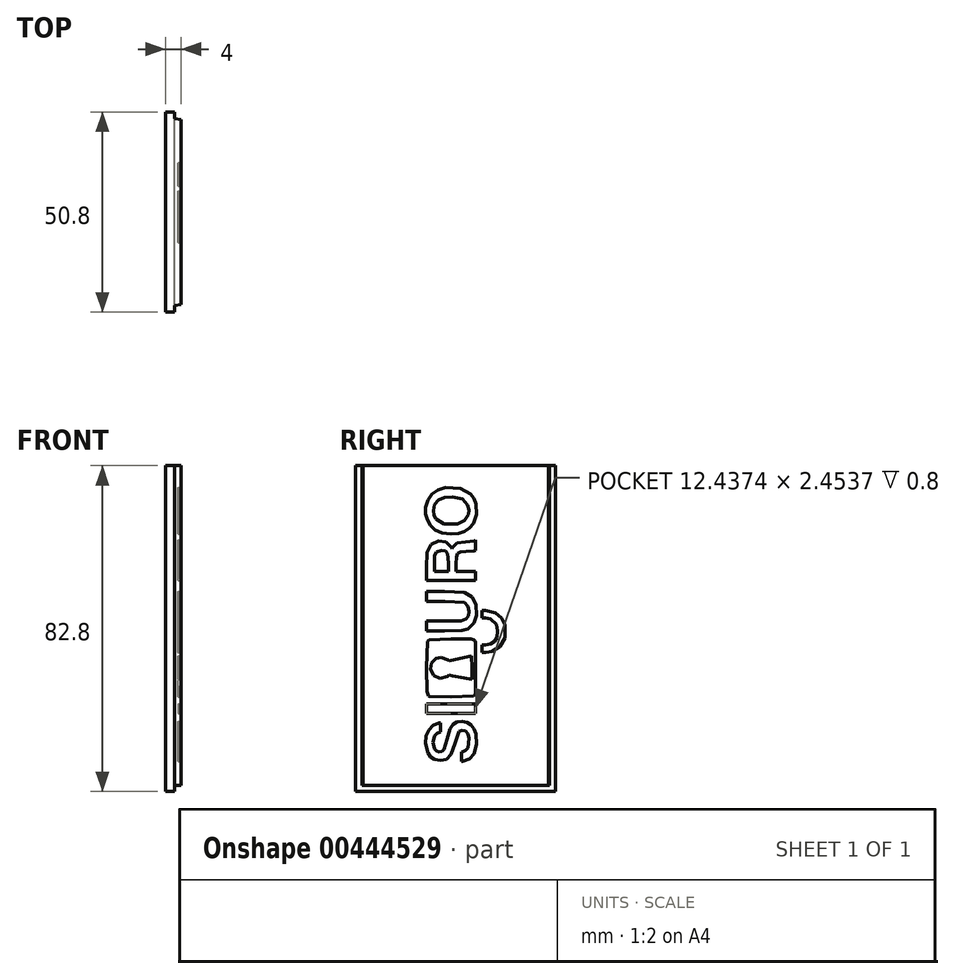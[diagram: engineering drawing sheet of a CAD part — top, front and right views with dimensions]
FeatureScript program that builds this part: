
annotation { "Feature Type Name" : "Feature", "Feature Type Description" : "" }
export const myFeature = defineFeature(function(context is Context, id is Id, definition is map)
    precondition{}
    {
        {
            var Q0;
            Q0=qCreatedBy(makeId("Top.planeOp"),FACE);
            var sketch = newSketch(context, id + "F0", { "sketchPlane" : qUnion([Q0])});
            skLineSegment(sketch, "E0.bottom", {"start": v(21.46, -52.97) * mm, "end": v(23.76, -52.97) * mm});
            skLineSegment(sketch, "E0.top", {"start": v(21.46, -2.17) * mm, "end": v(23.76, -2.17) * mm});
            skLineSegment(sketch, "E0.left", {"start": v(21.46, -52.97) * mm, "end": v(21.46, -2.17) * mm});
            skLineSegment(sketch, "E0.right", {"start": v(23.76, -52.97) * mm, "end": v(23.76, -2.17) * mm});
            skLineSegment(sketch, "E1", {"start": v(23.76, -52.97) * mm, "end": v(23.76, -51.37) * mm});
            skPoint(sketch, "E1.endSnap0", {"position": v(23.76, -27.57) * mm});
            skLineSegment(sketch, "E2", {"start": v(23.76, -51.37) * mm, "end": v(25.46, -51.37) * mm});
            skLineSegment(sketch, "E3", {"start": v(23.76, -2.17) * mm, "end": v(23.76, -3.77) * mm});
            skLineSegment(sketch, "E4", {"start": v(23.76, -3.77) * mm, "end": v(25.46, -3.77) * mm});
            skLineSegment(sketch, "E5", {"start": v(25.46, -51.37) * mm, "end": v(25.46, -3.77) * mm});
            skSolve(sketch);
        }
        {
            var Q0;
            Q0=makeQuery(id+"F0.imprint","IMPRINT",FACE,{"disambiguationData":[TD([[makeQuery(id+"F0.imprint","IMPRINT",EDGE,{"derivedFrom":sQuery(id+"F0.wireOp",EDGE,"E0.bottom")}),1.0]])]});
            var Q1;
            Q1=makeQuery(id+"F0.imprint","IMPRINT",FACE,{"disambiguationData":[TD([[makeQuery(id+"F0.imprint","IMPRINT",EDGE,{"derivedFrom":sQuery(id+"F0.wireOp",EDGE,"E0.right")}),-1.0]])]});
            extrude(context, id + "F1", {"entities" : qUnion([Q0, Q1]), "depth" : 82.8 * mm});
        }
        {
            var Q0;
            Q0=makeQuery(id+"F0.imprint","IMPRINT",FACE,{"disambiguationData":[TD([[makeQuery(id+"F0.imprint","IMPRINT",EDGE,{"derivedFrom":sQuery(id+"F0.wireOp",EDGE,"E0.right")}),-1.0]])]});
            extrude(context, id + "F2", {"entities" : qUnion([Q0]), "operationType" : NewBodyOperationType.REMOVE, "depth" : 1.5 * mm});
        }
        {
            var Q0;
            Q0=makeQuery(id+"F1.opExtrude","SWEPT_EDGE",EDGE,{"disambiguationData":[OSD([sQuery(id+"F0.wireOp",EDGE,"E2"),sQuery(id+"F0.wireOp",EDGE,"E5")])]});
            var Q1;
            Q1=makeQuery(id+"F2.boolean.opBoolean","COPY",EDGE,{"derivedFrom":makeQuery(id+"F2.opExtrude","CAP_EDGE",EDGE,{"disambiguationData":[OSD([sQuery(id+"F0.wireOp",EDGE,"E5")])],"isStart":false})});
            var Q2;
            Q2=makeQuery(id+"F1.opExtrude","SWEPT_EDGE",EDGE,{"disambiguationData":[OSD([sQuery(id+"F0.wireOp",EDGE,"E4"),sQuery(id+"F0.wireOp",EDGE,"E5")])]});
            chamfer(context, id + "F3", {"entities" : qUnion([Q0, Q1, Q2]), "chamferType" : ChamferType.OFFSET_ANGLE, "width" : 0.3 * mm, "oppositeDirection" : false, "angle" : 80 * degree, "tangentPropagation" : true});
        }
        {
            var Q0;
            Q0=makeQuery(id+"F1.opExtrude","SWEPT_FACE",FACE,{"disambiguationData":[OSD([sQuery(id+"F0.wireOp",EDGE,"E5")])]});
            var sketch = newSketch(context, id + "F4", { "sketchPlane" : qUnion([Q0])});
            skLineSegment(sketch, "E6", {"start": v(-14.78, 39.5) * mm, "end": v(-16, 36.81) * mm});
            skLineSegment(sketch, "E7", {"start": v(-16, 36.81) * mm, "end": v(-18.16, 35.38) * mm});
            skLineSegment(sketch, "E8", {"start": v(-18.16, 35.38) * mm, "end": v(-19.93, 35.18) * mm});
            skLineSegment(sketch, "E9", {"start": v(-19.93, 35.18) * mm, "end": v(-21.1, 35.18) * mm});
            skLineSegment(sketch, "E10", {"start": v(-21.1, 35.18) * mm, "end": v(-21.1, 36.32) * mm});
            skLineSegment(sketch, "E11", {"start": v(-21.1, 36.32) * mm, "end": v(-21.1, 37.46) * mm});
            skLineSegment(sketch, "E12", {"start": v(-21.1, 37.46) * mm, "end": v(-20.1, 37.5) * mm});
            skLineSegment(sketch, "E13", {"start": v(-20.1, 37.5) * mm, "end": v(-18.6, 37.79) * mm});
            skLineSegment(sketch, "E14", {"start": v(-18.6, 37.79) * mm, "end": v(-17.35, 39.11) * mm});
            skLineSegment(sketch, "E15", {"start": v(-17.35, 39.11) * mm, "end": v(-17.13, 40.68) * mm});
            skLineSegment(sketch, "E16", {"start": v(-17.13, 40.68) * mm, "end": v(-17.35, 42.25) * mm});
            skLineSegment(sketch, "E17", {"start": v(-17.35, 42.25) * mm, "end": v(-18.69, 43.58) * mm});
            skLineSegment(sketch, "E18", {"start": v(-18.69, 43.58) * mm, "end": v(-20.13, 43.85) * mm});
            skLineSegment(sketch, "E19", {"start": v(-20.13, 43.85) * mm, "end": v(-21.1, 43.9) * mm});
            skLineSegment(sketch, "E20", {"start": v(-21.1, 43.9) * mm, "end": v(-21.1, 45.04) * mm});
            skLineSegment(sketch, "E21", {"start": v(-21.1, 45.04) * mm, "end": v(-21.1, 46.18) * mm});
            skLineSegment(sketch, "E22", {"start": v(-21.1, 46.18) * mm, "end": v(-20, 46.17) * mm});
            skLineSegment(sketch, "E23", {"start": v(-20, 46.17) * mm, "end": v(-18.32, 45.99) * mm});
            skLineSegment(sketch, "E24", {"start": v(-18.32, 45.99) * mm, "end": v(-16.24, 44.73) * mm});
            skLineSegment(sketch, "E25", {"start": v(-16.24, 44.73) * mm, "end": v(-14.97, 42.67) * mm});
            skLineSegment(sketch, "E26", {"start": v(-14.97, 42.67) * mm, "end": v(-14.76, 40.93) * mm});
            skLineSegment(sketch, "E27", {"start": v(-14.76, 40.93) * mm, "end": v(-14.78, 39.5) * mm});
            skLineSegment(sketch, "E28", {"start": v(-14.78, 39.5) * mm, "end": v(-14.78, 39.5) * mm});
            skLineSegment(sketch, "E29", {"start": v(-15.1, 42.37) * mm, "end": v(-16, 44.13) * mm});
            skLineSegment(sketch, "E30", {"start": v(-16, 44.13) * mm, "end": v(-17.48, 45.4) * mm});
            skLineSegment(sketch, "E31", {"start": v(-17.48, 45.4) * mm, "end": v(-19.99, 45.97) * mm});
            skLineSegment(sketch, "E32", {"start": v(-19.99, 45.97) * mm, "end": v(-20.9, 45.97) * mm});
            skLineSegment(sketch, "E33", {"start": v(-20.9, 45.97) * mm, "end": v(-20.9, 45) * mm});
            skLineSegment(sketch, "E34", {"start": v(-20.9, 45) * mm, "end": v(-20.9, 44.02) * mm});
            skLineSegment(sketch, "E35", {"start": v(-20.9, 44.02) * mm, "end": v(-20.06, 44.02) * mm});
            skLineSegment(sketch, "E36", {"start": v(-20.06, 44.02) * mm, "end": v(-18.75, 43.85) * mm});
            skLineSegment(sketch, "E37", {"start": v(-18.75, 43.85) * mm, "end": v(-17.2, 42.43) * mm});
            skLineSegment(sketch, "E38", {"start": v(-17.2, 42.43) * mm, "end": v(-16.94, 40.8) * mm});
            skLineSegment(sketch, "E39", {"start": v(-16.94, 40.8) * mm, "end": v(-17.09, 39.19) * mm});
            skLineSegment(sketch, "E40", {"start": v(-17.09, 39.19) * mm, "end": v(-17.76, 38.12) * mm});
            skLineSegment(sketch, "E41", {"start": v(-17.76, 38.12) * mm, "end": v(-18.8, 37.46) * mm});
            skLineSegment(sketch, "E42", {"start": v(-18.8, 37.46) * mm, "end": v(-20.03, 37.28) * mm});
            skLineSegment(sketch, "E43", {"start": v(-20.03, 37.28) * mm, "end": v(-20.9, 37.23) * mm});
            skLineSegment(sketch, "E44", {"start": v(-20.9, 37.23) * mm, "end": v(-20.9, 36.25) * mm});
            skLineSegment(sketch, "E45", {"start": v(-20.9, 36.25) * mm, "end": v(-20.9, 35.28) * mm});
            skLineSegment(sketch, "E46", {"start": v(-20.9, 35.28) * mm, "end": v(-19.9, 35.33) * mm});
            skLineSegment(sketch, "E47", {"start": v(-19.9, 35.33) * mm, "end": v(-18.36, 35.55) * mm});
            skLineSegment(sketch, "E48", {"start": v(-18.36, 35.55) * mm, "end": v(-16.3, 36.84) * mm});
            skLineSegment(sketch, "E49", {"start": v(-16.3, 36.84) * mm, "end": v(-15.1, 38.95) * mm});
            skLineSegment(sketch, "E50", {"start": v(-15.1, 38.95) * mm, "end": v(-15.1, 42.37) * mm});
            skLineSegment(sketch, "E51", {"start": v(-0.1, -10) * mm, "end": v(-0.1, -10) * mm});
            skLineSegment(sketch, "E52", {"start": v(-22.14, 11.07) * mm, "end": v(-22.89, 9.2) * mm});
            skLineSegment(sketch, "E53", {"start": v(-22.89, 9.2) * mm, "end": v(-24.2, 7.95) * mm});
            skLineSegment(sketch, "E54", {"start": v(-24.2, 7.95) * mm, "end": v(-26, 7.47) * mm});
            skLineSegment(sketch, "E55", {"start": v(-26, 7.47) * mm, "end": v(-26.4, 7.47) * mm});
            skLineSegment(sketch, "E56", {"start": v(-26.4, 7.47) * mm, "end": v(-26.4, 8.81) * mm});
            skLineSegment(sketch, "E57", {"start": v(-26.4, 8.81) * mm, "end": v(-26.4, 10.15) * mm});
            skLineSegment(sketch, "E58", {"start": v(-26.4, 10.15) * mm, "end": v(-25.91, 10.26) * mm});
            skLineSegment(sketch, "E59", {"start": v(-25.91, 10.26) * mm, "end": v(-25.06, 10.73) * mm});
            skLineSegment(sketch, "E60", {"start": v(-25.06, 10.73) * mm, "end": v(-24.53, 11.58) * mm});
            skLineSegment(sketch, "E61", {"start": v(-24.53, 11.58) * mm, "end": v(-24.56, 14.2) * mm});
            skLineSegment(sketch, "E62", {"start": v(-24.56, 14.2) * mm, "end": v(-25.53, 15.23) * mm});
            skLineSegment(sketch, "E63", {"start": v(-25.53, 15.23) * mm, "end": v(-26.14, 15.25) * mm});
            skLineSegment(sketch, "E64", {"start": v(-26.14, 15.25) * mm, "end": v(-26.68, 14.9) * mm});
            skLineSegment(sketch, "E65", {"start": v(-26.68, 14.9) * mm, "end": v(-27.61, 11.97) * mm});
            skLineSegment(sketch, "E66", {"start": v(-27.61, 11.97) * mm, "end": v(-28.26, 9.72) * mm});
            skLineSegment(sketch, "E67", {"start": v(-28.26, 9.72) * mm, "end": v(-29.5, 8.15) * mm});
            skLineSegment(sketch, "E68", {"start": v(-29.5, 8.15) * mm, "end": v(-31.5, 7.64) * mm});
            skLineSegment(sketch, "E69", {"start": v(-31.5, 7.64) * mm, "end": v(-32.86, 7.87) * mm});
            skLineSegment(sketch, "E70", {"start": v(-32.86, 7.87) * mm, "end": v(-33.99, 8.52) * mm});
            skLineSegment(sketch, "E71", {"start": v(-33.99, 8.52) * mm, "end": v(-34.83, 9.57) * mm});
            skLineSegment(sketch, "E72", {"start": v(-34.83, 9.57) * mm, "end": v(-35.33, 10.95) * mm});
            skLineSegment(sketch, "E73", {"start": v(-35.33, 10.95) * mm, "end": v(-35.46, 12.63) * mm});
            skLineSegment(sketch, "E74", {"start": v(-35.46, 12.63) * mm, "end": v(-35.12, 14.9) * mm});
            skLineSegment(sketch, "E75", {"start": v(-35.12, 14.9) * mm, "end": v(-34.05, 16.51) * mm});
            skLineSegment(sketch, "E76", {"start": v(-34.05, 16.51) * mm, "end": v(-32.83, 17.33) * mm});
            skLineSegment(sketch, "E77", {"start": v(-32.83, 17.33) * mm, "end": v(-31.54, 17.62) * mm});
            skLineSegment(sketch, "E78", {"start": v(-31.54, 17.62) * mm, "end": v(-31.22, 17.62) * mm});
            skLineSegment(sketch, "E79", {"start": v(-31.22, 17.62) * mm, "end": v(-31.22, 16.27) * mm});
            skLineSegment(sketch, "E80", {"start": v(-31.22, 16.27) * mm, "end": v(-31.22, 14.92) * mm});
            skLineSegment(sketch, "E81", {"start": v(-31.22, 14.92) * mm, "end": v(-31.45, 14.87) * mm});
            skLineSegment(sketch, "E82", {"start": v(-31.45, 14.87) * mm, "end": v(-32.64, 14.16) * mm});
            skLineSegment(sketch, "E83", {"start": v(-32.64, 14.16) * mm, "end": v(-33.08, 12.36) * mm});
            skLineSegment(sketch, "E84", {"start": v(-33.08, 12.36) * mm, "end": v(-32.54, 10.71) * mm});
            skLineSegment(sketch, "E85", {"start": v(-32.54, 10.71) * mm, "end": v(-31.64, 10.35) * mm});
            skLineSegment(sketch, "E86", {"start": v(-31.64, 10.35) * mm, "end": v(-30.8, 10.78) * mm});
            skLineSegment(sketch, "E87", {"start": v(-30.8, 10.78) * mm, "end": v(-30.07, 13.24) * mm});
            skLineSegment(sketch, "E88", {"start": v(-30.07, 13.24) * mm, "end": v(-29.2, 16.16) * mm});
            skLineSegment(sketch, "E89", {"start": v(-29.2, 16.16) * mm, "end": v(-28.1, 17.53) * mm});
            skLineSegment(sketch, "E90", {"start": v(-28.1, 17.53) * mm, "end": v(-26.44, 18.03) * mm});
            skLineSegment(sketch, "E91", {"start": v(-26.44, 18.03) * mm, "end": v(-24.73, 17.8) * mm});
            skLineSegment(sketch, "E92", {"start": v(-24.73, 17.8) * mm, "end": v(-23.36, 16.97) * mm});
            skLineSegment(sketch, "E93", {"start": v(-23.36, 16.97) * mm, "end": v(-22.13, 14.48) * mm});
            skLineSegment(sketch, "E94", {"start": v(-22.13, 14.48) * mm, "end": v(-22.14, 11.07) * mm});
            skLineSegment(sketch, "E95", {"start": v(-31.4, -2.97) * mm, "end": v(-31.4, -2.97) * mm});
            skLineSegment(sketch, "E96", {"start": v(-22.38, 14.56) * mm, "end": v(-22.88, 15.85) * mm});
            skLineSegment(sketch, "E97", {"start": v(-22.88, 15.85) * mm, "end": v(-23.65, 16.85) * mm});
            skLineSegment(sketch, "E98", {"start": v(-23.65, 16.85) * mm, "end": v(-24.68, 17.54) * mm});
            skLineSegment(sketch, "E99", {"start": v(-24.68, 17.54) * mm, "end": v(-26.02, 17.77) * mm});
            skLineSegment(sketch, "E100", {"start": v(-26.02, 17.77) * mm, "end": v(-27.31, 17.65) * mm});
            skLineSegment(sketch, "E101", {"start": v(-27.31, 17.65) * mm, "end": v(-28.28, 17.05) * mm});
            skLineSegment(sketch, "E102", {"start": v(-28.28, 17.05) * mm, "end": v(-29.05, 15.87) * mm});
            skLineSegment(sketch, "E103", {"start": v(-29.05, 15.87) * mm, "end": v(-29.83, 13.2) * mm});
            skLineSegment(sketch, "E104", {"start": v(-29.83, 13.2) * mm, "end": v(-30.58, 10.66) * mm});
            skLineSegment(sketch, "E105", {"start": v(-30.58, 10.66) * mm, "end": v(-31.12, 10.21) * mm});
            skLineSegment(sketch, "E106", {"start": v(-31.12, 10.21) * mm, "end": v(-31.8, 10.1) * mm});
            skLineSegment(sketch, "E107", {"start": v(-31.8, 10.1) * mm, "end": v(-32.48, 10.33) * mm});
            skLineSegment(sketch, "E108", {"start": v(-32.48, 10.33) * mm, "end": v(-32.98, 10.87) * mm});
            skLineSegment(sketch, "E109", {"start": v(-32.98, 10.87) * mm, "end": v(-33.31, 12.47) * mm});
            skLineSegment(sketch, "E110", {"start": v(-33.31, 12.47) * mm, "end": v(-33, 14.05) * mm});
            skLineSegment(sketch, "E111", {"start": v(-33, 14.05) * mm, "end": v(-32.35, 14.78) * mm});
            skLineSegment(sketch, "E112", {"start": v(-32.35, 14.78) * mm, "end": v(-31.5, 15.09) * mm});
            skLineSegment(sketch, "E113", {"start": v(-31.5, 15.09) * mm, "end": v(-31.39, 16.26) * mm});
            skLineSegment(sketch, "E114", {"start": v(-31.39, 16.26) * mm, "end": v(-31.39, 17.43) * mm});
            skLineSegment(sketch, "E115", {"start": v(-31.39, 17.43) * mm, "end": v(-31.86, 17.35) * mm});
            skLineSegment(sketch, "E116", {"start": v(-31.86, 17.35) * mm, "end": v(-33.33, 16.8) * mm});
            skLineSegment(sketch, "E117", {"start": v(-33.33, 16.8) * mm, "end": v(-34.42, 15.7) * mm});
            skLineSegment(sketch, "E118", {"start": v(-34.42, 15.7) * mm, "end": v(-35.09, 14.14) * mm});
            skLineSegment(sketch, "E119", {"start": v(-35.09, 14.14) * mm, "end": v(-35.25, 12.24) * mm});
            skLineSegment(sketch, "E120", {"start": v(-35.25, 12.24) * mm, "end": v(-34.63, 9.74) * mm});
            skLineSegment(sketch, "E121", {"start": v(-34.63, 9.74) * mm, "end": v(-33.96, 8.84) * mm});
            skLineSegment(sketch, "E122", {"start": v(-33.96, 8.84) * mm, "end": v(-33.01, 8.2) * mm});
            skLineSegment(sketch, "E123", {"start": v(-33.01, 8.2) * mm, "end": v(-31.43, 7.94) * mm});
            skLineSegment(sketch, "E124", {"start": v(-31.43, 7.94) * mm, "end": v(-29.94, 8.17) * mm});
            skLineSegment(sketch, "E125", {"start": v(-29.94, 8.17) * mm, "end": v(-28.72, 9.37) * mm});
            skLineSegment(sketch, "E126", {"start": v(-28.72, 9.37) * mm, "end": v(-27.8, 12.24) * mm});
            skLineSegment(sketch, "E127", {"start": v(-27.8, 12.24) * mm, "end": v(-26.73, 15.22) * mm});
            skLineSegment(sketch, "E128", {"start": v(-26.73, 15.22) * mm, "end": v(-25.95, 15.49) * mm});
            skLineSegment(sketch, "E129", {"start": v(-25.95, 15.49) * mm, "end": v(-25.09, 15.32) * mm});
            skLineSegment(sketch, "E130", {"start": v(-25.09, 15.32) * mm, "end": v(-24.5, 14.62) * mm});
            skLineSegment(sketch, "E131", {"start": v(-24.5, 14.62) * mm, "end": v(-24.18, 13.5) * mm});
            skLineSegment(sketch, "E132", {"start": v(-24.18, 13.5) * mm, "end": v(-24.5, 11.05) * mm});
            skLineSegment(sketch, "E133", {"start": v(-24.5, 11.05) * mm, "end": v(-25.05, 10.38) * mm});
            skLineSegment(sketch, "E134", {"start": v(-25.05, 10.38) * mm, "end": v(-25.83, 10.04) * mm});
            skLineSegment(sketch, "E135", {"start": v(-25.83, 10.04) * mm, "end": v(-26.14, 9.99) * mm});
            skLineSegment(sketch, "E136", {"start": v(-26.14, 9.99) * mm, "end": v(-26.14, 8.82) * mm});
            skLineSegment(sketch, "E137", {"start": v(-26.14, 8.82) * mm, "end": v(-26.14, 7.64) * mm});
            skLineSegment(sketch, "E138", {"start": v(-26.14, 7.64) * mm, "end": v(-25.87, 7.69) * mm});
            skLineSegment(sketch, "E139", {"start": v(-25.87, 7.69) * mm, "end": v(-24.13, 8.3) * mm});
            skLineSegment(sketch, "E140", {"start": v(-24.13, 8.3) * mm, "end": v(-22.97, 9.54) * mm});
            skLineSegment(sketch, "E141", {"start": v(-22.97, 9.54) * mm, "end": v(-22.25, 11.9) * mm});
            skLineSegment(sketch, "E142", {"start": v(-22.25, 11.9) * mm, "end": v(-22.38, 14.56) * mm});
            skLineSegment(sketch, "E143", {"start": v(-22.13, 44.1) * mm, "end": v(-23.35, 41.76) * mm});
            skLineSegment(sketch, "E144", {"start": v(-23.35, 41.76) * mm, "end": v(-24.31, 41.06) * mm});
            skLineSegment(sketch, "E145", {"start": v(-24.31, 41.06) * mm, "end": v(-26.02, 40.63) * mm});
            skLineSegment(sketch, "E146", {"start": v(-26.02, 40.63) * mm, "end": v(-30.71, 40.57) * mm});
            skLineSegment(sketch, "E147", {"start": v(-30.71, 40.57) * mm, "end": v(-35.15, 40.6) * mm});
            skLineSegment(sketch, "E148", {"start": v(-35.15, 40.6) * mm, "end": v(-35.15, 42) * mm});
            skLineSegment(sketch, "E149", {"start": v(-35.15, 42) * mm, "end": v(-35.15, 43.39) * mm});
            skLineSegment(sketch, "E150", {"start": v(-35.15, 43.39) * mm, "end": v(-30.67, 43.43) * mm});
            skLineSegment(sketch, "E151", {"start": v(-30.67, 43.43) * mm, "end": v(-26.19, 43.56) * mm});
            skLineSegment(sketch, "E152", {"start": v(-26.19, 43.56) * mm, "end": v(-25, 44.14) * mm});
            skLineSegment(sketch, "E153", {"start": v(-25, 44.14) * mm, "end": v(-24.45, 45.73) * mm});
            skLineSegment(sketch, "E154", {"start": v(-24.45, 45.73) * mm, "end": v(-24.72, 47.05) * mm});
            skLineSegment(sketch, "E155", {"start": v(-24.72, 47.05) * mm, "end": v(-25.54, 47.82) * mm});
            skLineSegment(sketch, "E156", {"start": v(-25.54, 47.82) * mm, "end": v(-26.02, 48.04) * mm});
            skLineSegment(sketch, "E157", {"start": v(-26.02, 48.04) * mm, "end": v(-30.59, 48.08) * mm});
            skLineSegment(sketch, "E158", {"start": v(-30.59, 48.08) * mm, "end": v(-35.15, 48.13) * mm});
            skLineSegment(sketch, "E159", {"start": v(-35.15, 48.13) * mm, "end": v(-35.15, 49.52) * mm});
            skLineSegment(sketch, "E160", {"start": v(-35.15, 49.52) * mm, "end": v(-35.15, 50.92) * mm});
            skLineSegment(sketch, "E161", {"start": v(-35.15, 50.92) * mm, "end": v(-30.6, 50.94) * mm});
            skLineSegment(sketch, "E162", {"start": v(-30.6, 50.94) * mm, "end": v(-25.94, 50.89) * mm});
            skLineSegment(sketch, "E163", {"start": v(-25.94, 50.89) * mm, "end": v(-24.28, 50.44) * mm});
            skLineSegment(sketch, "E164", {"start": v(-24.28, 50.44) * mm, "end": v(-22.91, 49.24) * mm});
            skLineSegment(sketch, "E165", {"start": v(-22.91, 49.24) * mm, "end": v(-22.13, 47.39) * mm});
            skLineSegment(sketch, "E166", {"start": v(-22.13, 47.39) * mm, "end": v(-22.13, 44.1) * mm});
            skLineSegment(sketch, "E167", {"start": v(-22.13, 44.1) * mm, "end": v(-22.13, 44.1) * mm});
            skLineSegment(sketch, "E168", {"start": v(-22.38, 47.45) * mm, "end": v(-23.44, 49.47) * mm});
            skLineSegment(sketch, "E169", {"start": v(-23.44, 49.47) * mm, "end": v(-25.35, 50.6) * mm});
            skLineSegment(sketch, "E170", {"start": v(-25.35, 50.6) * mm, "end": v(-30.4, 50.77) * mm});
            skLineSegment(sketch, "E171", {"start": v(-30.4, 50.77) * mm, "end": v(-34.94, 50.8) * mm});
            skLineSegment(sketch, "E172", {"start": v(-34.94, 50.8) * mm, "end": v(-34.94, 49.53) * mm});
            skLineSegment(sketch, "E173", {"start": v(-34.94, 49.53) * mm, "end": v(-34.94, 48.26) * mm});
            skLineSegment(sketch, "E174", {"start": v(-34.94, 48.26) * mm, "end": v(-30.31, 48.23) * mm});
            skLineSegment(sketch, "E175", {"start": v(-30.31, 48.23) * mm, "end": v(-25.34, 48.03) * mm});
            skLineSegment(sketch, "E176", {"start": v(-25.34, 48.03) * mm, "end": v(-24.44, 47.02) * mm});
            skLineSegment(sketch, "E177", {"start": v(-24.44, 47.02) * mm, "end": v(-24.24, 45.71) * mm});
            skLineSegment(sketch, "E178", {"start": v(-24.24, 45.71) * mm, "end": v(-24.38, 44.57) * mm});
            skLineSegment(sketch, "E179", {"start": v(-24.38, 44.57) * mm, "end": v(-24.96, 43.83) * mm});
            skLineSegment(sketch, "E180", {"start": v(-24.96, 43.83) * mm, "end": v(-26.2, 43.34) * mm});
            skLineSegment(sketch, "E181", {"start": v(-26.2, 43.34) * mm, "end": v(-30.61, 43.26) * mm});
            skLineSegment(sketch, "E182", {"start": v(-30.61, 43.26) * mm, "end": v(-34.94, 43.26) * mm});
            skLineSegment(sketch, "E183", {"start": v(-34.94, 43.26) * mm, "end": v(-34.94, 42.03) * mm});
            skLineSegment(sketch, "E184", {"start": v(-34.94, 42.03) * mm, "end": v(-34.94, 40.8) * mm});
            skLineSegment(sketch, "E185", {"start": v(-34.94, 40.8) * mm, "end": v(-30.48, 40.8) * mm});
            skLineSegment(sketch, "E186", {"start": v(-30.48, 40.8) * mm, "end": v(-25.97, 40.88) * mm});
            skLineSegment(sketch, "E187", {"start": v(-25.97, 40.88) * mm, "end": v(-24.41, 41.28) * mm});
            skLineSegment(sketch, "E188", {"start": v(-24.41, 41.28) * mm, "end": v(-22.9, 42.75) * mm});
            skLineSegment(sketch, "E189", {"start": v(-22.9, 42.75) * mm, "end": v(-22.25, 44.69) * mm});
            skLineSegment(sketch, "E190", {"start": v(-22.25, 44.69) * mm, "end": v(-22.38, 47.45) * mm});
            skLineSegment(sketch, "E191", {"start": v(4.98, -2.73) * mm, "end": v(4.98, -2.73) * mm});
            skLineSegment(sketch, "E192", {"start": v(-22.12, 69.86) * mm, "end": v(-22.69, 68.28) * mm});
            skLineSegment(sketch, "E193", {"start": v(-22.69, 68.28) * mm, "end": v(-23.6, 67.01) * mm});
            skLineSegment(sketch, "E194", {"start": v(-23.6, 67.01) * mm, "end": v(-24.86, 66.05) * mm});
            skLineSegment(sketch, "E195", {"start": v(-24.86, 66.05) * mm, "end": v(-26.44, 65.41) * mm});
            skLineSegment(sketch, "E196", {"start": v(-26.44, 65.41) * mm, "end": v(-28.72, 65.23) * mm});
            skLineSegment(sketch, "E197", {"start": v(-28.72, 65.23) * mm, "end": v(-30.8, 65.36) * mm});
            skLineSegment(sketch, "E198", {"start": v(-30.8, 65.36) * mm, "end": v(-32.4, 65.95) * mm});
            skLineSegment(sketch, "E199", {"start": v(-32.4, 65.95) * mm, "end": v(-33.8, 66.98) * mm});
            skLineSegment(sketch, "E200", {"start": v(-33.8, 66.98) * mm, "end": v(-35.06, 68.9) * mm});
            skLineSegment(sketch, "E201", {"start": v(-35.06, 68.9) * mm, "end": v(-35.46, 71.34) * mm});
            skLineSegment(sketch, "E202", {"start": v(-35.46, 71.34) * mm, "end": v(-34.8, 74.31) * mm});
            skLineSegment(sketch, "E203", {"start": v(-34.8, 74.31) * mm, "end": v(-33.31, 76.18) * mm});
            skLineSegment(sketch, "E204", {"start": v(-33.31, 76.18) * mm, "end": v(-31, 77.29) * mm});
            skLineSegment(sketch, "E205", {"start": v(-31, 77.29) * mm, "end": v(-28.72, 77.47) * mm});
            skLineSegment(sketch, "E206", {"start": v(-28.72, 77.47) * mm, "end": v(-26.44, 77.29) * mm});
            skLineSegment(sketch, "E207", {"start": v(-26.44, 77.29) * mm, "end": v(-23.79, 75.86) * mm});
            skLineSegment(sketch, "E208", {"start": v(-23.79, 75.86) * mm, "end": v(-22.88, 74.74) * mm});
            skLineSegment(sketch, "E209", {"start": v(-22.88, 74.74) * mm, "end": v(-22.25, 73.34) * mm});
            skLineSegment(sketch, "E210", {"start": v(-22.25, 73.34) * mm, "end": v(-22.12, 69.86) * mm});
            skLineSegment(sketch, "E211", {"start": v(-22.43, 73.05) * mm, "end": v(-23, 74.45) * mm});
            skLineSegment(sketch, "E212", {"start": v(-23, 74.45) * mm, "end": v(-23.84, 75.58) * mm});
            skLineSegment(sketch, "E213", {"start": v(-23.84, 75.58) * mm, "end": v(-26.4, 77.02) * mm});
            skLineSegment(sketch, "E214", {"start": v(-26.4, 77.02) * mm, "end": v(-30.2, 77.2) * mm});
            skLineSegment(sketch, "E215", {"start": v(-30.2, 77.2) * mm, "end": v(-32.11, 76.62) * mm});
            skLineSegment(sketch, "E216", {"start": v(-32.11, 76.62) * mm, "end": v(-33.6, 75.59) * mm});
            skLineSegment(sketch, "E217", {"start": v(-33.6, 75.59) * mm, "end": v(-34.64, 74.1) * mm});
            skLineSegment(sketch, "E218", {"start": v(-34.64, 74.1) * mm, "end": v(-35.2, 72.2) * mm});
            skLineSegment(sketch, "E219", {"start": v(-35.2, 72.2) * mm, "end": v(-35.21, 70.54) * mm});
            skLineSegment(sketch, "E220", {"start": v(-35.21, 70.54) * mm, "end": v(-34.79, 68.94) * mm});
            skLineSegment(sketch, "E221", {"start": v(-34.79, 68.94) * mm, "end": v(-33.98, 67.54) * mm});
            skLineSegment(sketch, "E222", {"start": v(-33.98, 67.54) * mm, "end": v(-32.85, 66.48) * mm});
            skLineSegment(sketch, "E223", {"start": v(-32.85, 66.48) * mm, "end": v(-31.04, 65.68) * mm});
            skLineSegment(sketch, "E224", {"start": v(-31.04, 65.68) * mm, "end": v(-28.71, 65.43) * mm});
            skLineSegment(sketch, "E225", {"start": v(-28.71, 65.43) * mm, "end": v(-26.86, 65.58) * mm});
            skLineSegment(sketch, "E226", {"start": v(-26.86, 65.58) * mm, "end": v(-25.33, 66.06) * mm});
            skLineSegment(sketch, "E227", {"start": v(-25.33, 66.06) * mm, "end": v(-24.09, 66.89) * mm});
            skLineSegment(sketch, "E228", {"start": v(-24.09, 66.89) * mm, "end": v(-23.1, 68.06) * mm});
            skLineSegment(sketch, "E229", {"start": v(-23.1, 68.06) * mm, "end": v(-22.25, 70.42) * mm});
            skLineSegment(sketch, "E230", {"start": v(-22.25, 70.42) * mm, "end": v(-22.43, 73.05) * mm});
            skLineSegment(sketch, "E231", {"start": v(-24.3, 70.42) * mm, "end": v(-25.28, 68.85) * mm});
            skLineSegment(sketch, "E232", {"start": v(-25.28, 68.85) * mm, "end": v(-27.07, 67.95) * mm});
            skLineSegment(sketch, "E233", {"start": v(-27.07, 67.95) * mm, "end": v(-30.54, 68) * mm});
            skLineSegment(sketch, "E234", {"start": v(-30.54, 68) * mm, "end": v(-32.55, 69.22) * mm});
            skLineSegment(sketch, "E235", {"start": v(-32.55, 69.22) * mm, "end": v(-33.07, 70.18) * mm});
            skLineSegment(sketch, "E236", {"start": v(-33.07, 70.18) * mm, "end": v(-33.25, 71.35) * mm});
            skLineSegment(sketch, "E237", {"start": v(-33.25, 71.35) * mm, "end": v(-32.9, 72.9) * mm});
            skLineSegment(sketch, "E238", {"start": v(-32.9, 72.9) * mm, "end": v(-31.93, 74.05) * mm});
            skLineSegment(sketch, "E239", {"start": v(-31.93, 74.05) * mm, "end": v(-30.38, 74.72) * mm});
            skLineSegment(sketch, "E240", {"start": v(-30.38, 74.72) * mm, "end": v(-28.34, 74.88) * mm});
            skLineSegment(sketch, "E241", {"start": v(-28.34, 74.88) * mm, "end": v(-25.9, 74.3) * mm});
            skLineSegment(sketch, "E242", {"start": v(-25.9, 74.3) * mm, "end": v(-24.52, 72.82) * mm});
            skLineSegment(sketch, "E243", {"start": v(-24.52, 72.82) * mm, "end": v(-24.23, 71.53) * mm});
            skLineSegment(sketch, "E244", {"start": v(-24.23, 71.53) * mm, "end": v(-24.3, 70.42) * mm});
            skLineSegment(sketch, "E245", {"start": v(-24.73, 72.72) * mm, "end": v(-26.21, 74.16) * mm});
            skLineSegment(sketch, "E246", {"start": v(-26.21, 74.16) * mm, "end": v(-28.72, 74.65) * mm});
            skLineSegment(sketch, "E247", {"start": v(-28.72, 74.65) * mm, "end": v(-30.68, 74.4) * mm});
            skLineSegment(sketch, "E248", {"start": v(-30.68, 74.4) * mm, "end": v(-32.08, 73.57) * mm});
            skLineSegment(sketch, "E249", {"start": v(-32.08, 73.57) * mm, "end": v(-32.78, 72.56) * mm});
            skLineSegment(sketch, "E250", {"start": v(-32.78, 72.56) * mm, "end": v(-33.03, 71.38) * mm});
            skLineSegment(sketch, "E251", {"start": v(-33.03, 71.38) * mm, "end": v(-32.82, 70.2) * mm});
            skLineSegment(sketch, "E252", {"start": v(-32.82, 70.2) * mm, "end": v(-32.15, 69.16) * mm});
            skLineSegment(sketch, "E253", {"start": v(-32.15, 69.16) * mm, "end": v(-30.74, 68.32) * mm});
            skLineSegment(sketch, "E254", {"start": v(-30.74, 68.32) * mm, "end": v(-28.72, 68.05) * mm});
            skLineSegment(sketch, "E255", {"start": v(-28.72, 68.05) * mm, "end": v(-26.8, 68.3) * mm});
            skLineSegment(sketch, "E256", {"start": v(-26.8, 68.3) * mm, "end": v(-25.42, 69.08) * mm});
            skLineSegment(sketch, "E257", {"start": v(-25.42, 69.08) * mm, "end": v(-24.66, 70.12) * mm});
            skLineSegment(sketch, "E258", {"start": v(-24.66, 70.12) * mm, "end": v(-24.48, 71.48) * mm});
            skLineSegment(sketch, "E259", {"start": v(-24.48, 71.48) * mm, "end": v(-24.73, 72.72) * mm});
            skLineSegment(sketch, "E260", {"start": v(-28.74, 19.68) * mm, "end": v(-35.15, 19.7) * mm});
            skLineSegment(sketch, "E261", {"start": v(-35.15, 19.7) * mm, "end": v(-35.18, 21.02) * mm});
            skLineSegment(sketch, "E262", {"start": v(-35.18, 21.02) * mm, "end": v(-35.08, 22.43) * mm});
            skLineSegment(sketch, "E263", {"start": v(-35.08, 22.43) * mm, "end": v(-28.67, 22.51) * mm});
            skLineSegment(sketch, "E264", {"start": v(-28.67, 22.51) * mm, "end": v(-22.38, 22.49) * mm});
            skLineSegment(sketch, "E265", {"start": v(-22.38, 22.49) * mm, "end": v(-22.36, 21.07) * mm});
            skLineSegment(sketch, "E266", {"start": v(-22.36, 21.07) * mm, "end": v(-22.33, 19.65) * mm});
            skLineSegment(sketch, "E267", {"start": v(-22.33, 19.65) * mm, "end": v(-28.74, 19.68) * mm});
            skLineSegment(sketch, "E268", {"start": v(-22.8, 3.63) * mm, "end": v(-22.8, 3.63) * mm});
            skLineSegment(sketch, "E269", {"start": v(-28.72, 22.28) * mm, "end": v(-34.94, 22.28) * mm});
            skLineSegment(sketch, "E270", {"start": v(-34.94, 22.28) * mm, "end": v(-34.94, 21.05) * mm});
            skLineSegment(sketch, "E271", {"start": v(-34.94, 21.05) * mm, "end": v(-34.94, 19.82) * mm});
            skLineSegment(sketch, "E272", {"start": v(-34.94, 19.82) * mm, "end": v(-28.72, 19.82) * mm});
            skLineSegment(sketch, "E273", {"start": v(-28.72, 19.82) * mm, "end": v(-22.5, 19.82) * mm});
            skLineSegment(sketch, "E274", {"start": v(-22.5, 19.82) * mm, "end": v(-22.5, 21.05) * mm});
            skLineSegment(sketch, "E275", {"start": v(-22.5, 21.05) * mm, "end": v(-22.5, 22.28) * mm});
            skLineSegment(sketch, "E276", {"start": v(-22.5, 22.28) * mm, "end": v(-28.72, 22.28) * mm});
            skLineSegment(sketch, "E277", {"start": v(-22.53, 24.48) * mm, "end": v(-22.96, 24.02) * mm});
            skLineSegment(sketch, "E278", {"start": v(-22.96, 24.02) * mm, "end": v(-28.67, 23.84) * mm});
            skLineSegment(sketch, "E279", {"start": v(-28.67, 23.84) * mm, "end": v(-34.44, 24.02) * mm});
            skLineSegment(sketch, "E280", {"start": v(-34.44, 24.02) * mm, "end": v(-34.92, 24.47) * mm});
            skLineSegment(sketch, "E281", {"start": v(-34.92, 24.47) * mm, "end": v(-35.11, 24.76) * mm});
            skLineSegment(sketch, "E282", {"start": v(-35.11, 24.76) * mm, "end": v(-35.11, 31.35) * mm});
            skLineSegment(sketch, "E283", {"start": v(-35.11, 31.35) * mm, "end": v(-35.05, 37.62) * mm});
            skLineSegment(sketch, "E284", {"start": v(-35.05, 37.62) * mm, "end": v(-34.9, 38.42) * mm});
            skLineSegment(sketch, "E285", {"start": v(-34.9, 38.42) * mm, "end": v(-34.57, 38.71) * mm});
            skLineSegment(sketch, "E286", {"start": v(-34.57, 38.71) * mm, "end": v(-34.3, 38.9) * mm});
            skLineSegment(sketch, "E287", {"start": v(-34.3, 38.9) * mm, "end": v(-28.8, 38.92) * mm});
            skLineSegment(sketch, "E288", {"start": v(-28.8, 38.92) * mm, "end": v(-23.52, 38.88) * mm});
            skLineSegment(sketch, "E289", {"start": v(-23.52, 38.88) * mm, "end": v(-22.82, 38.71) * mm});
            skLineSegment(sketch, "E290", {"start": v(-22.82, 38.71) * mm, "end": v(-22.53, 38.36) * mm});
            skLineSegment(sketch, "E291", {"start": v(-22.53, 38.36) * mm, "end": v(-22.34, 38.07) * mm});
            skLineSegment(sketch, "E292", {"start": v(-22.34, 38.07) * mm, "end": v(-22.34, 31.41) * mm});
            skLineSegment(sketch, "E293", {"start": v(-22.34, 31.41) * mm, "end": v(-22.34, 24.76) * mm});
            skLineSegment(sketch, "E294", {"start": v(-22.34, 24.76) * mm, "end": v(-22.53, 24.48) * mm});
            skLineSegment(sketch, "E295", {"start": v(-22.7, 38.2) * mm, "end": v(-22.99, 38.54) * mm});
            skLineSegment(sketch, "E296", {"start": v(-22.99, 38.54) * mm, "end": v(-23.68, 38.71) * mm});
            skLineSegment(sketch, "E297", {"start": v(-23.68, 38.71) * mm, "end": v(-28.82, 38.76) * mm});
            skLineSegment(sketch, "E298", {"start": v(-28.82, 38.76) * mm, "end": v(-34.4, 38.56) * mm});
            skLineSegment(sketch, "E299", {"start": v(-34.4, 38.56) * mm, "end": v(-34.8, 38.1) * mm});
            skLineSegment(sketch, "E300", {"start": v(-34.8, 38.1) * mm, "end": v(-34.94, 31.43) * mm});
            skLineSegment(sketch, "E301", {"start": v(-34.94, 31.43) * mm, "end": v(-34.9, 25.45) * mm});
            skLineSegment(sketch, "E302", {"start": v(-34.9, 25.45) * mm, "end": v(-34.48, 24.3) * mm});
            skLineSegment(sketch, "E303", {"start": v(-34.48, 24.3) * mm, "end": v(-34.25, 24.1) * mm});
            skLineSegment(sketch, "E304", {"start": v(-34.25, 24.1) * mm, "end": v(-28.8, 24.07) * mm});
            skLineSegment(sketch, "E305", {"start": v(-28.8, 24.07) * mm, "end": v(-23.06, 24.22) * mm});
            skLineSegment(sketch, "E306", {"start": v(-23.06, 24.22) * mm, "end": v(-22.73, 24.49) * mm});
            skLineSegment(sketch, "E307", {"start": v(-22.73, 24.49) * mm, "end": v(-22.57, 25.26) * mm});
            skLineSegment(sketch, "E308", {"start": v(-22.57, 25.26) * mm, "end": v(-22.5, 31.42) * mm});
            skLineSegment(sketch, "E309", {"start": v(-22.5, 31.42) * mm, "end": v(-22.5, 37.9) * mm});
            skLineSegment(sketch, "E310", {"start": v(-22.5, 37.9) * mm, "end": v(-22.7, 38.2) * mm});
            skLineSegment(sketch, "E311", {"start": v(-4.28, -2.41) * mm, "end": v(-4.28, -2.41) * mm});
            skLineSegment(sketch, "E312", {"start": v(-23.5, 28.42) * mm, "end": v(-25.5, 28.8) * mm});
            skLineSegment(sketch, "E313", {"start": v(-25.5, 28.8) * mm, "end": v(-28.34, 29.4) * mm});
            skLineSegment(sketch, "E314", {"start": v(-28.34, 29.4) * mm, "end": v(-29.25, 29.57) * mm});
            skLineSegment(sketch, "E315", {"start": v(-29.25, 29.57) * mm, "end": v(-29.64, 29.27) * mm});
            skLineSegment(sketch, "E316", {"start": v(-29.64, 29.27) * mm, "end": v(-31.5, 28.73) * mm});
            skLineSegment(sketch, "E317", {"start": v(-31.5, 28.73) * mm, "end": v(-33.22, 29.48) * mm});
            skLineSegment(sketch, "E318", {"start": v(-33.22, 29.48) * mm, "end": v(-34, 31.19) * mm});
            skLineSegment(sketch, "E319", {"start": v(-34, 31.19) * mm, "end": v(-33.68, 32.72) * mm});
            skLineSegment(sketch, "E320", {"start": v(-33.68, 32.72) * mm, "end": v(-32.54, 33.78) * mm});
            skLineSegment(sketch, "E321", {"start": v(-32.54, 33.78) * mm, "end": v(-31.31, 34.08) * mm});
            skLineSegment(sketch, "E322", {"start": v(-31.31, 34.08) * mm, "end": v(-29.54, 33.46) * mm});
            skLineSegment(sketch, "E323", {"start": v(-29.54, 33.46) * mm, "end": v(-29.23, 33.2) * mm});
            skLineSegment(sketch, "E324", {"start": v(-29.23, 33.2) * mm, "end": v(-26.48, 33.8) * mm});
            skLineSegment(sketch, "E325", {"start": v(-26.48, 33.8) * mm, "end": v(-23.58, 34.37) * mm});
            skLineSegment(sketch, "E326", {"start": v(-23.58, 34.37) * mm, "end": v(-23.44, 31.42) * mm});
            skLineSegment(sketch, "E327", {"start": v(-23.44, 31.42) * mm, "end": v(-23.5, 28.42) * mm});
            skLineSegment(sketch, "E328", {"start": v(-26.33, 33.6) * mm, "end": v(-29.22, 33.03) * mm});
            skLineSegment(sketch, "E329", {"start": v(-29.22, 33.03) * mm, "end": v(-29.64, 33.25) * mm});
            skLineSegment(sketch, "E330", {"start": v(-29.64, 33.25) * mm, "end": v(-31.31, 33.87) * mm});
            skLineSegment(sketch, "E331", {"start": v(-31.31, 33.87) * mm, "end": v(-32.95, 33.27) * mm});
            skLineSegment(sketch, "E332", {"start": v(-32.95, 33.27) * mm, "end": v(-33.65, 32.24) * mm});
            skLineSegment(sketch, "E333", {"start": v(-33.65, 32.24) * mm, "end": v(-33.77, 31.08) * mm});
            skLineSegment(sketch, "E334", {"start": v(-33.77, 31.08) * mm, "end": v(-33.34, 29.98) * mm});
            skLineSegment(sketch, "E335", {"start": v(-33.34, 29.98) * mm, "end": v(-32.37, 29.15) * mm});
            skLineSegment(sketch, "E336", {"start": v(-32.37, 29.15) * mm, "end": v(-30.95, 28.95) * mm});
            skLineSegment(sketch, "E337", {"start": v(-30.95, 28.95) * mm, "end": v(-29.64, 29.57) * mm});
            skLineSegment(sketch, "E338", {"start": v(-29.64, 29.57) * mm, "end": v(-29.37, 29.83) * mm});
            skLineSegment(sketch, "E339", {"start": v(-29.37, 29.83) * mm, "end": v(-26.68, 29.26) * mm});
            skLineSegment(sketch, "E340", {"start": v(-26.68, 29.26) * mm, "end": v(-23.8, 28.65) * mm});
            skLineSegment(sketch, "E341", {"start": v(-23.8, 28.65) * mm, "end": v(-23.6, 28.6) * mm});
            skLineSegment(sketch, "E342", {"start": v(-23.6, 28.6) * mm, "end": v(-23.6, 31.4) * mm});
            skLineSegment(sketch, "E343", {"start": v(-23.6, 31.4) * mm, "end": v(-23.6, 34.18) * mm});
            skLineSegment(sketch, "E344", {"start": v(-23.6, 34.18) * mm, "end": v(-26.33, 33.6) * mm});
            skLineSegment(sketch, "E345", {"start": v(-28.75, 53.35) * mm, "end": v(-35.15, 53.37) * mm});
            skLineSegment(sketch, "E346", {"start": v(-35.15, 53.37) * mm, "end": v(-35.15, 57) * mm});
            skLineSegment(sketch, "E347", {"start": v(-35.15, 57) * mm, "end": v(-35.09, 60.67) * mm});
            skLineSegment(sketch, "E348", {"start": v(-35.09, 60.67) * mm, "end": v(-34.69, 62.05) * mm});
            skLineSegment(sketch, "E349", {"start": v(-34.69, 62.05) * mm, "end": v(-33.32, 63.47) * mm});
            skLineSegment(sketch, "E350", {"start": v(-33.32, 63.47) * mm, "end": v(-31.23, 63.88) * mm});
            skLineSegment(sketch, "E351", {"start": v(-31.23, 63.88) * mm, "end": v(-29.7, 63.52) * mm});
            skLineSegment(sketch, "E352", {"start": v(-29.7, 63.52) * mm, "end": v(-28.68, 62.57) * mm});
            skLineSegment(sketch, "E353", {"start": v(-28.68, 62.57) * mm, "end": v(-28.44, 62.2) * mm});
            skLineSegment(sketch, "E354", {"start": v(-28.44, 62.2) * mm, "end": v(-28.32, 62.44) * mm});
            skLineSegment(sketch, "E355", {"start": v(-28.32, 62.44) * mm, "end": v(-27.29, 63.32) * mm});
            skLineSegment(sketch, "E356", {"start": v(-27.29, 63.32) * mm, "end": v(-25.1, 63.57) * mm});
            skLineSegment(sketch, "E357", {"start": v(-25.1, 63.57) * mm, "end": v(-23.36, 63.7) * mm});
            skLineSegment(sketch, "E358", {"start": v(-23.36, 63.7) * mm, "end": v(-22.87, 64.04) * mm});
            skLineSegment(sketch, "E359", {"start": v(-22.87, 64.04) * mm, "end": v(-22.58, 64.16) * mm});
            skLineSegment(sketch, "E360", {"start": v(-22.58, 64.16) * mm, "end": v(-22.34, 64.16) * mm});
            skLineSegment(sketch, "E361", {"start": v(-22.34, 64.16) * mm, "end": v(-22.34, 62.6) * mm});
            skLineSegment(sketch, "E362", {"start": v(-22.34, 62.6) * mm, "end": v(-22.34, 61.04) * mm});
            skLineSegment(sketch, "E363", {"start": v(-22.34, 61.04) * mm, "end": v(-22.65, 60.94) * mm});
            skLineSegment(sketch, "E364", {"start": v(-22.65, 60.94) * mm, "end": v(-24.58, 60.77) * mm});
            skLineSegment(sketch, "E365", {"start": v(-24.58, 60.77) * mm, "end": v(-26.1, 60.64) * mm});
            skLineSegment(sketch, "E366", {"start": v(-26.1, 60.64) * mm, "end": v(-26.89, 60.28) * mm});
            skLineSegment(sketch, "E367", {"start": v(-26.89, 60.28) * mm, "end": v(-27.2, 59.42) * mm});
            skLineSegment(sketch, "E368", {"start": v(-27.2, 59.42) * mm, "end": v(-27.24, 57.8) * mm});
            skLineSegment(sketch, "E369", {"start": v(-27.24, 57.8) * mm, "end": v(-27.24, 56.12) * mm});
            skLineSegment(sketch, "E370", {"start": v(-27.24, 56.12) * mm, "end": v(-24.8, 56.12) * mm});
            skLineSegment(sketch, "E371", {"start": v(-24.8, 56.12) * mm, "end": v(-22.34, 56.12) * mm});
            skLineSegment(sketch, "E372", {"start": v(-22.34, 56.12) * mm, "end": v(-22.34, 54.72) * mm});
            skLineSegment(sketch, "E373", {"start": v(-22.34, 54.72) * mm, "end": v(-22.34, 53.33) * mm});
            skLineSegment(sketch, "E374", {"start": v(-22.34, 53.33) * mm, "end": v(-28.75, 53.35) * mm});
            skLineSegment(sketch, "E375", {"start": v(10.88, 3.63) * mm, "end": v(10.88, 3.63) * mm});
            skLineSegment(sketch, "E376", {"start": v(-25.01, 55.95) * mm, "end": v(-27.52, 55.95) * mm});
            skLineSegment(sketch, "E377", {"start": v(-27.52, 55.95) * mm, "end": v(-27.48, 57.83) * mm});
            skLineSegment(sketch, "E378", {"start": v(-27.48, 57.83) * mm, "end": v(-27.4, 59.56) * mm});
            skLineSegment(sketch, "E379", {"start": v(-27.4, 59.56) * mm, "end": v(-27.1, 60.46) * mm});
            skLineSegment(sketch, "E380", {"start": v(-27.1, 60.46) * mm, "end": v(-26.36, 60.84) * mm});
            skLineSegment(sketch, "E381", {"start": v(-26.36, 60.84) * mm, "end": v(-24.94, 60.95) * mm});
            skLineSegment(sketch, "E382", {"start": v(-24.94, 60.95) * mm, "end": v(-22.97, 61.11) * mm});
            skLineSegment(sketch, "E383", {"start": v(-22.97, 61.11) * mm, "end": v(-22.5, 61.2) * mm});
            skLineSegment(sketch, "E384", {"start": v(-22.5, 61.2) * mm, "end": v(-22.5, 62.56) * mm});
            skLineSegment(sketch, "E385", {"start": v(-22.5, 62.56) * mm, "end": v(-22.57, 63.9) * mm});
            skLineSegment(sketch, "E386", {"start": v(-22.57, 63.9) * mm, "end": v(-22.83, 63.7) * mm});
            skLineSegment(sketch, "E387", {"start": v(-22.83, 63.7) * mm, "end": v(-25.09, 63.36) * mm});
            skLineSegment(sketch, "E388", {"start": v(-25.09, 63.36) * mm, "end": v(-27.2, 63.1) * mm});
            skLineSegment(sketch, "E389", {"start": v(-27.2, 63.1) * mm, "end": v(-28.16, 62.2) * mm});
            skLineSegment(sketch, "E390", {"start": v(-28.16, 62.2) * mm, "end": v(-28.48, 61.8) * mm});
            skLineSegment(sketch, "E391", {"start": v(-28.48, 61.8) * mm, "end": v(-28.73, 62.13) * mm});
            skLineSegment(sketch, "E392", {"start": v(-28.73, 62.13) * mm, "end": v(-30.04, 63.4) * mm});
            skLineSegment(sketch, "E393", {"start": v(-30.04, 63.4) * mm, "end": v(-31.99, 63.66) * mm});
            skLineSegment(sketch, "E394", {"start": v(-31.99, 63.66) * mm, "end": v(-33.9, 62.7) * mm});
            skLineSegment(sketch, "E395", {"start": v(-33.9, 62.7) * mm, "end": v(-34.86, 60.74) * mm});
            skLineSegment(sketch, "E396", {"start": v(-34.86, 60.74) * mm, "end": v(-34.94, 56.96) * mm});
            skLineSegment(sketch, "E397", {"start": v(-34.94, 56.96) * mm, "end": v(-34.94, 53.58) * mm});
            skLineSegment(sketch, "E398", {"start": v(-34.94, 53.58) * mm, "end": v(-28.72, 53.58) * mm});
            skLineSegment(sketch, "E399", {"start": v(-28.72, 53.58) * mm, "end": v(-22.5, 53.58) * mm});
            skLineSegment(sketch, "E400", {"start": v(-22.5, 53.58) * mm, "end": v(-22.5, 54.77) * mm});
            skLineSegment(sketch, "E401", {"start": v(-22.5, 54.77) * mm, "end": v(-22.5, 55.95) * mm});
            skLineSegment(sketch, "E402", {"start": v(-22.5, 55.95) * mm, "end": v(-25.01, 55.95) * mm});
            skLineSegment(sketch, "E403", {"start": v(-31.17, 55.95) * mm, "end": v(-33, 55.95) * mm});
            skLineSegment(sketch, "E404", {"start": v(-33, 55.95) * mm, "end": v(-33, 57.84) * mm});
            skLineSegment(sketch, "E405", {"start": v(-33, 57.84) * mm, "end": v(-32.9, 59.98) * mm});
            skLineSegment(sketch, "E406", {"start": v(-32.9, 59.98) * mm, "end": v(-32.47, 60.83) * mm});
            skLineSegment(sketch, "E407", {"start": v(-32.47, 60.83) * mm, "end": v(-31.15, 61.28) * mm});
            skLineSegment(sketch, "E408", {"start": v(-31.15, 61.28) * mm, "end": v(-30.2, 61.1) * mm});
            skLineSegment(sketch, "E409", {"start": v(-30.2, 61.1) * mm, "end": v(-29.62, 60.48) * mm});
            skLineSegment(sketch, "E410", {"start": v(-29.62, 60.48) * mm, "end": v(-29.37, 58) * mm});
            skLineSegment(sketch, "E411", {"start": v(-29.37, 58) * mm, "end": v(-29.35, 55.95) * mm});
            skLineSegment(sketch, "E412", {"start": v(-29.35, 55.95) * mm, "end": v(-31.17, 55.95) * mm});
            skLineSegment(sketch, "E413", {"start": v(-29.83, 60.35) * mm, "end": v(-30.9, 61.06) * mm});
            skLineSegment(sketch, "E414", {"start": v(-30.9, 61.06) * mm, "end": v(-32.2, 60.76) * mm});
            skLineSegment(sketch, "E415", {"start": v(-32.2, 60.76) * mm, "end": v(-32.65, 60.02) * mm});
            skLineSegment(sketch, "E416", {"start": v(-32.65, 60.02) * mm, "end": v(-32.74, 58) * mm});
            skLineSegment(sketch, "E417", {"start": v(-32.74, 58) * mm, "end": v(-32.74, 56.12) * mm});
            skLineSegment(sketch, "E418", {"start": v(-32.74, 56.12) * mm, "end": v(-31.17, 56.12) * mm});
            skLineSegment(sketch, "E419", {"start": v(-31.17, 56.12) * mm, "end": v(-29.6, 56.12) * mm});
            skLineSegment(sketch, "E420", {"start": v(-29.6, 56.12) * mm, "end": v(-29.63, 58.09) * mm});
            skLineSegment(sketch, "E421", {"start": v(-29.63, 58.09) * mm, "end": v(-29.83, 60.35) * mm});
            skLineSegment(sketch, "E422", {"start": v(-29.83, 60.35) * mm, "end": v(-29.83, 60.35) * mm});
            skSolve(sketch);
        }
        {
            var Q0;
            Q0=makeQuery(id+"F4.imprint","IMPRINT",FACE,{"disambiguationData":[TD([[makeQuery(id+"F4.imprint","IMPRINT",EDGE,{"derivedFrom":sQuery(id+"F4.wireOp",EDGE,"E269")}),1.0]])]});
            var Q1;
            Q1=makeQuery(id+"F4.imprint","IMPRINT",FACE,{"disambiguationData":[TD([[makeQuery(id+"F4.imprint","IMPRINT",EDGE,{"derivedFrom":sQuery(id+"F4.wireOp",EDGE,"E96")}),1.0]])]});
            var Q2;
            Q2=makeQuery(id+"F4.imprint","IMPRINT",FACE,{"disambiguationData":[TD([[makeQuery(id+"F4.imprint","IMPRINT",EDGE,{"derivedFrom":sQuery(id+"F4.wireOp",EDGE,"E295")}),1.0]])]});
            var Q3;
            Q3=makeQuery(id+"F4.imprint","IMPRINT",FACE,{"disambiguationData":[TD([[makeQuery(id+"F4.imprint","IMPRINT",EDGE,{"derivedFrom":sQuery(id+"F4.wireOp",EDGE,"E29")}),1.0]])]});
            var Q4;
            Q4=makeQuery(id+"F4.imprint","IMPRINT",FACE,{"disambiguationData":[TD([[makeQuery(id+"F4.imprint","IMPRINT",EDGE,{"derivedFrom":sQuery(id+"F4.wireOp",EDGE,"E168")}),1.0]])]});
            var Q5;
            Q5=makeQuery(id+"F4.imprint","IMPRINT",FACE,{"disambiguationData":[TD([[makeQuery(id+"F4.imprint","IMPRINT",EDGE,{"derivedFrom":sQuery(id+"F4.wireOp",EDGE,"E376")}),1.0]])]});
            var Q6;
            Q6=makeQuery(id+"F4.imprint","IMPRINT",FACE,{"disambiguationData":[TD([[makeQuery(id+"F4.imprint","IMPRINT",EDGE,{"derivedFrom":sQuery(id+"F4.wireOp",EDGE,"E211")}),1.0]])]});
            extrude(context, id + "F5", {"entities" : qUnion([Q0, Q1, Q2, Q3, Q4, Q5, Q6]), "operationType" : NewBodyOperationType.REMOVE, "oppositeDirection" : true, "depth" : 0.8 * mm});
        }
    });
